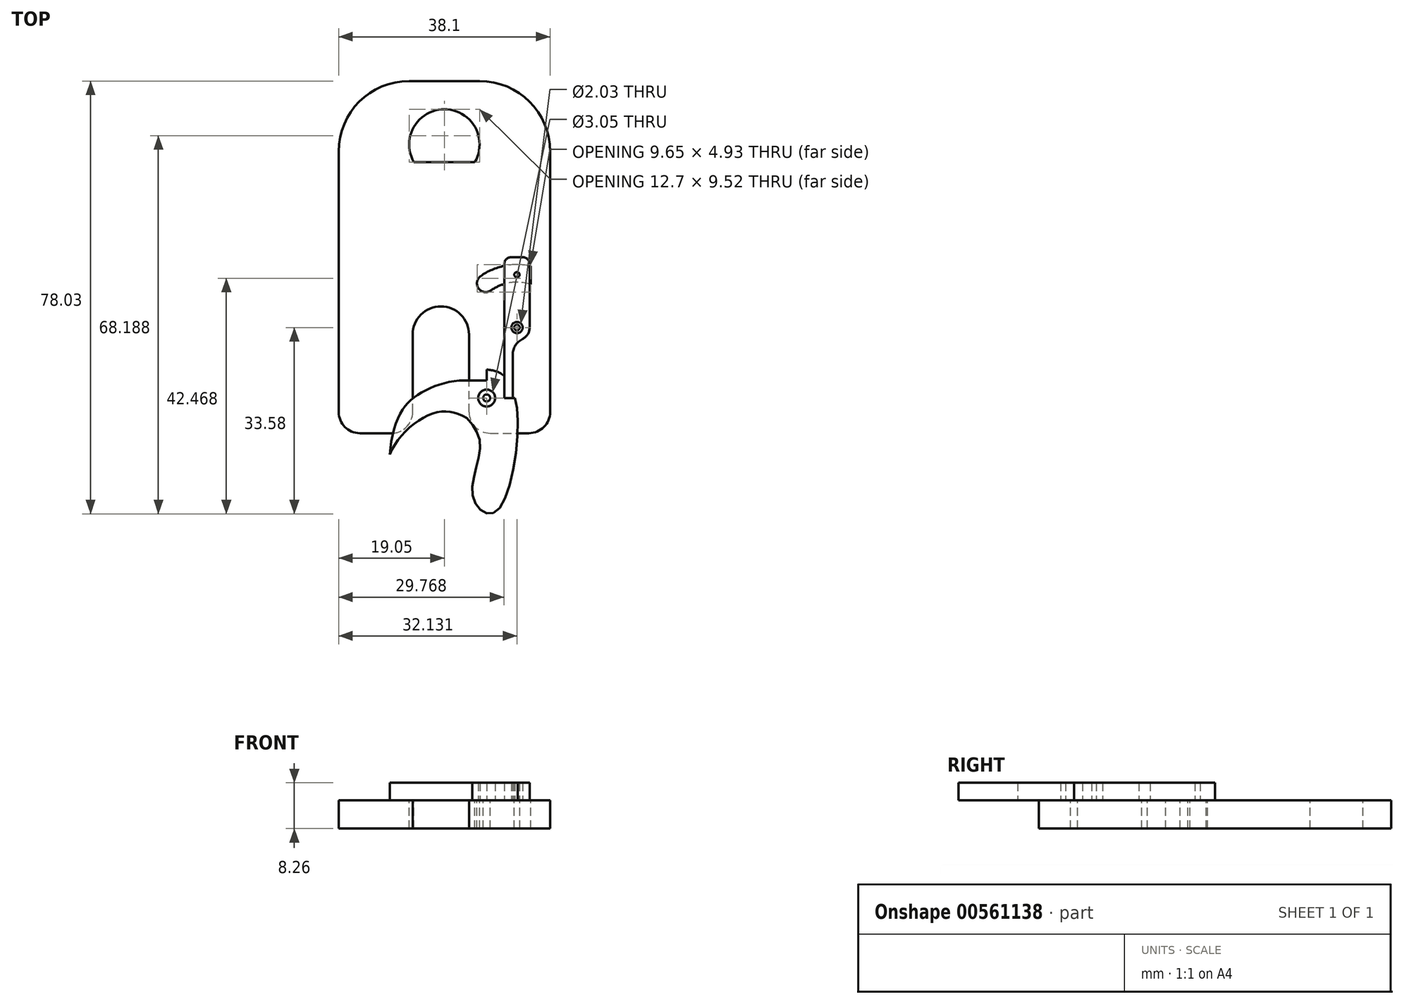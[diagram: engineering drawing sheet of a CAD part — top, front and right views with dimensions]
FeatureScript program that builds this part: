
annotation { "Feature Type Name" : "Feature", "Feature Type Description" : "" }
export const myFeature = defineFeature(function(context is Context, id is Id, definition is map)
    precondition{}
    {
        {
            var Q0;
            Q0=qCreatedBy(makeId("Top.planeOp"),FACE);
            var sketch = newSketch(context, id + "F0", { "sketchPlane" : qUnion([Q0])});
            skCircle(sketch, "E0", {"center": v(0, 0) * mm, "radius": 15.88 * mm, "construction": true});
            skEllipse(sketch, "E1", {"center": v(0, 0) * mm, "majorRadius": 12.7 * mm, "minorRadius": 7.62 * mm, "majorAxis": v(0.7, 0.7), "construction": true});
            skCircle(sketch, "E2", {"center": v(7.62, 7.62) * mm, "radius": 1.52 * mm});
            skLineSegment(sketch, "E3", {"start": v(-8.98, -8.98) * mm, "end": v(8.98, 8.98) * mm, "construction": true});
            skCircle(sketch, "E4", {"center": v(7.62, 7.62) * mm, "radius": 5.1 * mm, "construction": true});
            skLineSegment(sketch, "E5", {"start": v(12.72, 7.62) * mm, "end": v(10.8, 7.62) * mm});
            skLineSegment(sketch, "E6", {"start": v(10.8, 7.62) * mm, "end": v(10.8, 11.6) * mm});
            skArc(sketch, "E7", {"start": v(10.8, 11.6) * mm, "mid": v(9.3, 12.43) * mm, "end": v(7.62, 12.72) * mm});
            skCircle(sketch, "E8", {"center": v(7.62, 7.62) * mm, "radius": 2.98 * mm, "construction": true});
            skCircle(sketch, "E9", {"center": v(7.62, 7.62) * mm, "radius": 21.04 * mm, "construction": true});
            skFitSpline(sketch, "E10", {"points": [v(4.01, 4.01) * mm, v(-2.71, 1.83) * mm, v(-6.43, -8.04) * mm, v(-6.6, -9.02) * mm, v(-8.92, -8.19) * mm, v(-8.76, 2.93) * mm, v(-4.46, 8.4) * mm, v(3.63, 10.8) * mm], "startDerivative": vector(-47.69, -1.45) * mm, "endDerivative": vector(53.95, 0) * mm});
            skFitSpline(sketch, "E11.trimOffspring", {"points": [v(-10.38, -6.12) * mm, v(-1.13, 5.08) * mm, v(3.97, 4.05) * mm, v(4.01, 4.01) * mm, v(6.36, 0) * mm, v(5.13, -10.16) * mm, v(9.24, -12.9) * mm, v(12.72, 7.62) * mm], "startDerivative": vector(-10.72, 64.76) * mm, "endDerivative": vector(-17.22, 48.63) * mm});
            skLineSegment(sketch, "E12", {"start": v(3.63, 10.8) * mm, "end": v(7.62, 10.8) * mm});
            skLineSegment(sketch, "E13", {"start": v(7.62, 12.72) * mm, "end": v(7.62, 10.8) * mm});
            skLineSegment(sketch, "E14", {"start": v(7.62, 7.62) * mm, "end": v(7.62, 14.2) * mm, "construction": true});
            skSolve(sketch);
        }
        {
            var Q0;
            Q0=makeQuery(id+"F0.imprint","IMPRINT",FACE,{"disambiguationData":[TD([[makeQuery(id+"F0.imprint","IMPRINT",EDGE,{"derivedFrom":sQuery(id+"F0.wireOp",EDGE,"E2")}),-1.0]])]});
            extrude(context, id + "F1", {"entities" : qUnion([Q0]), "depth" : 3.17 * mm});
        }
        {
            var Q0;
            Q0=qCreatedBy(makeId("Top.planeOp"),FACE);
            var sketch = newSketch(context, id + "F2", { "sketchPlane" : qUnion([Q0])});
            skLineSegment(sketch, "E15.bottom", {"start": v(-6.35, 64.77) * mm, "end": v(6.35, 64.77) * mm});
            skLineSegment(sketch, "E15.top", {"start": v(-15.24, 1.27) * mm, "end": v(-9.53, 1.27) * mm});
            skLineSegment(sketch, "E15.left", {"start": v(-19.05, 52.07) * mm, "end": v(-19.05, 5.08) * mm});
            skLineSegment(sketch, "E15.right", {"start": v(19.05, 52.07) * mm, "end": v(19.05, 5.08) * mm});
            skLineSegment(sketch, "E16.top", {"start": v(-5.72, 19.05) * mm, "end": v(4.44, 19.05) * mm});
            skLineSegment(sketch, "E16.left", {"start": v(-5.72, 5.08) * mm, "end": v(-5.72, 19.05) * mm});
            skLineSegment(sketch, "E16.right", {"start": v(4.45, 5.08) * mm, "end": v(4.44, 19.05) * mm});
            skLineSegment(sketch, "E17", {"start": v(0, 0) * mm, "end": v(0, 39.33) * mm, "construction": true});
            skLineSegment(sketch, "E18.trimOffspring", {"start": v(8.26, 1.27) * mm, "end": v(15.24, 1.27) * mm});
            skCircle(sketch, "E19", {"center": v(7.62, 7.62) * mm, "radius": 0.64 * mm});
            skPoint(sketch, "E20.visualSharp", {"position": v(-19.05, 64.77) * mm});
            skArc(sketch, "E20.filletArc", {"start": v(-6.35, 64.77) * mm, "mid": v(-15.33, 61.05) * mm, "end": v(-19.05, 52.07) * mm});
            skPoint(sketch, "E21.visualSharp", {"position": v(19.05, 64.77) * mm});
            skArc(sketch, "E21.filletArc", {"start": v(19.05, 52.07) * mm, "mid": v(15.33, 61.05) * mm, "end": v(6.35, 64.77) * mm});
            skArc(sketch, "E22", {"start": v(5.5, 50.17) * mm, "mid": v(0, 59.7) * mm, "end": v(-5.5, 50.17) * mm});
            skLineSegment(sketch, "E23", {"start": v(-5.5, 50.17) * mm, "end": v(5.5, 50.17) * mm});
            skArc(sketch, "E24", {"start": v(4.44, 19.05) * mm, "mid": v(-0.64, 24.13) * mm, "end": v(-5.72, 19.05) * mm});
            skPoint(sketch, "E25.visualSharp", {"position": v(-19.05, 1.27) * mm});
            skArc(sketch, "E25.filletArc", {"start": v(-19.05, 5.08) * mm, "mid": v(-17.93, 2.39) * mm, "end": v(-15.24, 1.27) * mm});
            skPoint(sketch, "E26.visualSharp", {"position": v(-5.72, 1.27) * mm});
            skArc(sketch, "E26.filletArc", {"start": v(-9.53, 1.27) * mm, "mid": v(-6.83, 2.39) * mm, "end": v(-5.72, 5.08) * mm});
            skPoint(sketch, "E27.visualSharp", {"position": v(4.45, 1.27) * mm});
            skArc(sketch, "E27.filletArc", {"start": v(4.45, 5.08) * mm, "mid": v(5.56, 2.39) * mm, "end": v(8.26, 1.27) * mm});
            skPoint(sketch, "E28.visualSharp", {"position": v(19.05, 1.27) * mm});
            skArc(sketch, "E28.filletArc", {"start": v(15.24, 1.27) * mm, "mid": v(17.93, 2.39) * mm, "end": v(19.05, 5.08) * mm});
            skSolve(sketch);
        }
        {
            var Q0;
            Q0=makeQuery(id+"F2.imprint","IMPRINT",FACE,{"disambiguationData":[TD([[makeQuery(id+"F2.imprint","IMPRINT",EDGE,{"derivedFrom":sQuery(id+"F2.wireOp",EDGE,"E15.bottom")}),-1.0]])]});
            extrude(context, id + "F3", {"entities" : qUnion([Q0]), "oppositeDirection" : true, "depth" : 5.08 * mm});
        }
        {
            var Q0;
            Q0=makeQuery(id+"F3.opExtrude","CAP_FACE",FACE,{"disambiguationData":[OSD([sQuery(id+"F2.wireOp",EDGE,"E15.bottom"),sQuery(id+"F2.wireOp",EDGE,"E15.top"),sQuery(id+"F2.wireOp",EDGE,"E15.left"),sQuery(id+"F2.wireOp",EDGE,"E15.right"),sQuery(id+"F2.wireOp",EDGE,"E16.top"),sQuery(id+"F2.wireOp",EDGE,"E16.left"),sQuery(id+"F2.wireOp",EDGE,"E16.right"),sQuery(id+"F2.wireOp",EDGE,"E18.trimOffspring"),sQuery(id+"F2.wireOp",EDGE,"E19")])],"isStart":true});
            var sketch = newSketch(context, id + "F4", { "sketchPlane" : qUnion([Q0])});
            skLineSegment(sketch, "E29.bottom", {"start": v(10.8, 7.62) * mm, "end": v(12.32, 7.62) * mm});
            skLineSegment(sketch, "E29.top", {"start": v(12.06, 33.02) * mm, "end": v(14.1, 33.02) * mm});
            skLineSegment(sketch, "E29.left", {"start": v(10.8, 7.62) * mm, "end": v(10.8, 31.75) * mm});
            skLineSegment(sketch, "E29.right", {"start": v(15.37, 20.32) * mm, "end": v(15.37, 31.75) * mm});
            skLineSegment(sketch, "E30", {"start": v(13.08, 33.02) * mm, "end": v(13.08, 7.62) * mm, "construction": true});
            skCircle(sketch, "E31", {"center": v(13.08, 20.32) * mm, "radius": 1.02 * mm});
            skLineSegment(sketch, "E32", {"start": v(12.32, 7.62) * mm, "end": v(12.32, 15.42) * mm});
            skArc(sketch, "E33", {"start": v(14.1, 18.27) * mm, "mid": v(15.02, 19.11) * mm, "end": v(15.37, 20.32) * mm});
            skCircle(sketch, "E34", {"center": v(13.08, 29.85) * mm, "radius": 0.48 * mm});
            skPoint(sketch, "E35.orphan", {"position": v(15.37, 7.62) * mm});
            skPoint(sketch, "E36.visualSharp", {"position": v(12.32, 18.16) * mm});
            skArc(sketch, "E36.filletArc", {"start": v(14.1, 18.27) * mm, "mid": v(12.8, 17.1) * mm, "end": v(12.32, 15.42) * mm});
            skPoint(sketch, "E37.visualSharp", {"position": v(10.8, 33.02) * mm});
            skArc(sketch, "E37.filletArc", {"start": v(12.06, 33.02) * mm, "mid": v(11.17, 32.65) * mm, "end": v(10.8, 31.75) * mm});
            skPoint(sketch, "E38.visualSharp", {"position": v(15.37, 33.02) * mm});
            skArc(sketch, "E38.filletArc", {"start": v(15.37, 31.75) * mm, "mid": v(15, 32.65) * mm, "end": v(14.1, 33.02) * mm});
            skSolve(sketch);
        }
        {
            var Q0;
            Q0=qSketchRegion(id+"F4",true);
            extrude(context, id + "F5", {"entities" : qUnion([Q0]), "depth" : 3.17 * mm});
        }
        {
            var Q0;
            Q0=sQuery(id+"F4.wireOp",VERTEX,"E33.center");
            var Q1;
            Q1=makeQuery(id+"F3.opExtrude","SWEPT_BODY",BODY,{"disambiguationData":[OSD([sQuery(id+"F2.wireOp",EDGE,"E15.bottom"),sQuery(id+"F2.wireOp",EDGE,"E15.top"),sQuery(id+"F2.wireOp",EDGE,"E15.left"),sQuery(id+"F2.wireOp",EDGE,"E15.right"),sQuery(id+"F2.wireOp",EDGE,"E16.top"),sQuery(id+"F2.wireOp",EDGE,"E16.left"),sQuery(id+"F2.wireOp",EDGE,"E16.right"),sQuery(id+"F2.wireOp",EDGE,"E18.trimOffspring"),sQuery(id+"F2.wireOp",EDGE,"E19")])]});
            hole(context, id + "F6", {"style" : HoleStyle.SIMPLE, "endStyle" : HoleEndStyle.THROUGH, "holeDiameter" : 1.02 * mm, "isTappedThrough" : true, "tappedDepth" : 12.7 * mm, "tapClearance" : 3, "locations" : qUnion([Q0]), "scope" : qUnion([Q1])});
        }
        {
            var Q0;
            Q0=makeQuery(id+"F3.opExtrude","CAP_FACE",FACE,{"disambiguationData":[OSD([sQuery(id+"F2.wireOp",EDGE,"E15.bottom"),sQuery(id+"F2.wireOp",EDGE,"E15.top"),sQuery(id+"F2.wireOp",EDGE,"E15.left"),sQuery(id+"F2.wireOp",EDGE,"E15.right"),sQuery(id+"F2.wireOp",EDGE,"E16.top"),sQuery(id+"F2.wireOp",EDGE,"E16.left"),sQuery(id+"F2.wireOp",EDGE,"E16.right"),sQuery(id+"F2.wireOp",EDGE,"E18.trimOffspring"),sQuery(id+"F2.wireOp",EDGE,"E19")])],"isStart":true});
            var sketch = newSketch(context, id + "F7", { "sketchPlane" : qUnion([Q0])});
            skArc(sketch, "E39", {"start": v(15.54, 31.4) * mm, "mid": v(10.85, 31.45) * mm, "end": v(6.54, 29.6) * mm});
            skArc(sketch, "E40", {"start": v(15.54, 28.12) * mm, "mid": v(11.83, 28.4) * mm, "end": v(8.37, 27) * mm});
            skArc(sketch, "E41", {"start": v(6.54, 29.6) * mm, "mid": v(6.16, 27.4) * mm, "end": v(8.37, 27) * mm});
            skLineSegment(sketch, "E42", {"start": v(15.54, 31.4) * mm, "end": v(15.54, 28.12) * mm});
            skSolve(sketch);
        }
        {
            var Q0;
            Q0=makeQuery(id+"F7.imprint","IMPRINT",FACE,{"disambiguationData":[TD([[makeQuery(id+"F7.imprint","IMPRINT",EDGE,{"derivedFrom":sQuery(id+"F7.wireOp",EDGE,"E39")}),1.0]])]});
            extrude(context, id + "F8", {"entities" : qUnion([Q0]), "operationType" : NewBodyOperationType.REMOVE, "oppositeDirection" : true, "depth" : 25.4 * mm});
        }
    });
